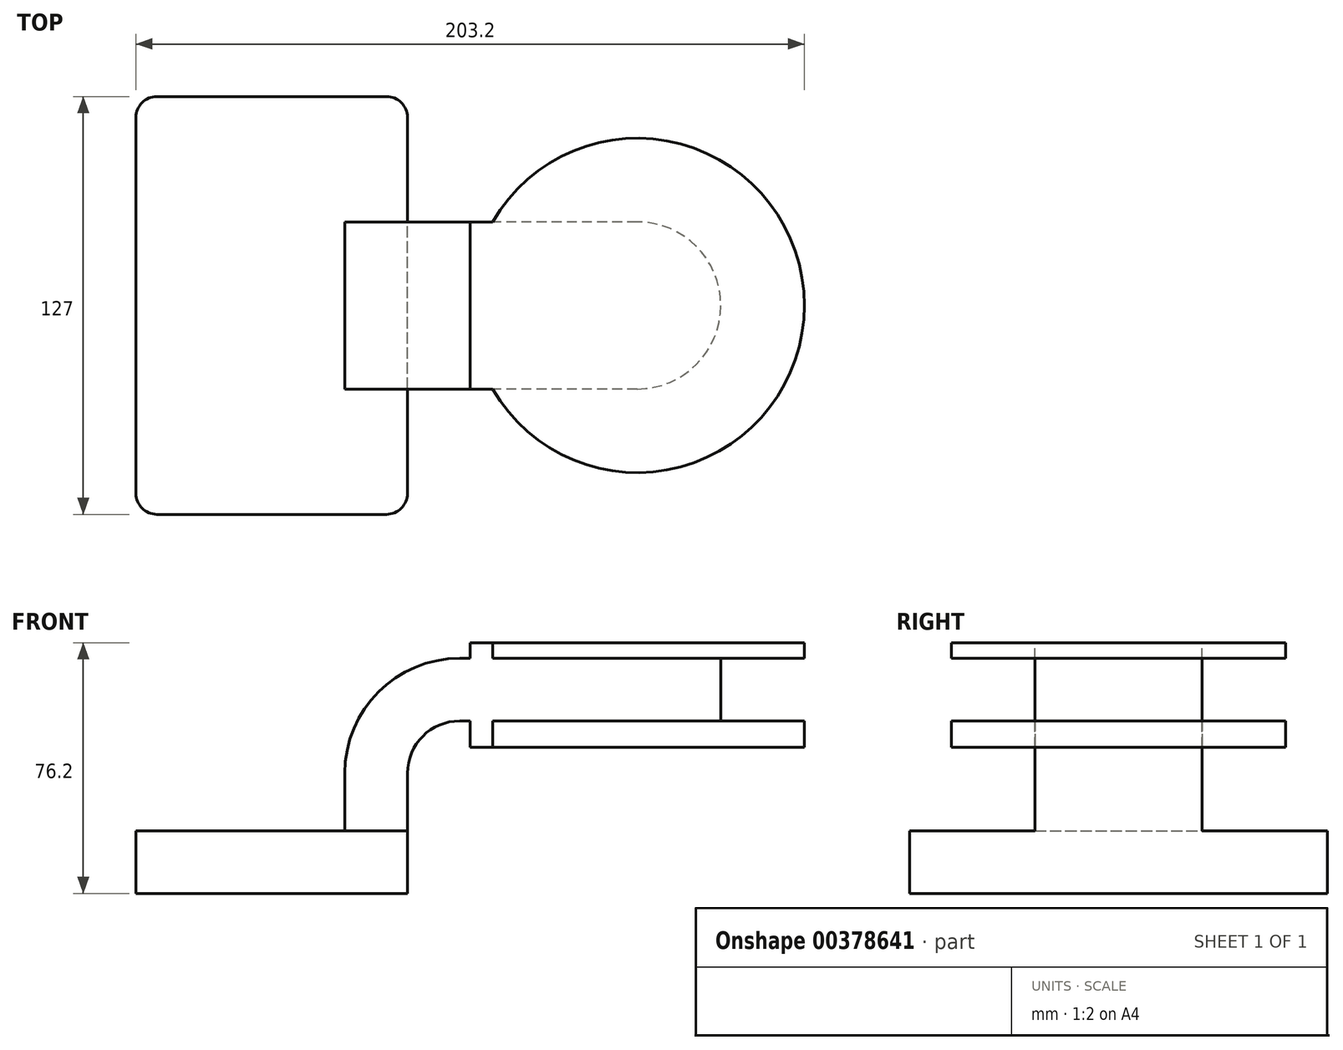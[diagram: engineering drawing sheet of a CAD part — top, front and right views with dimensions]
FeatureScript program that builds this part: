
annotation { "Feature Type Name" : "Feature", "Feature Type Description" : "" }
export const myFeature = defineFeature(function(context is Context, id is Id, definition is map)
    precondition{}
    {
        {
            var Q0;
            Q0=qCreatedBy(makeId("Front.planeOp"),FACE);
            var sketch = newSketch(context, id + "F0", { "sketchPlane" : qUnion([Q0])});
            skLineSegment(sketch, "E0.bottom", {"start": v(-41.27, -9.53) * mm, "end": v(41.28, -9.53) * mm});
            skLineSegment(sketch, "E0.top", {"start": v(-41.28, 9.53) * mm, "end": v(41.28, 9.53) * mm});
            skLineSegment(sketch, "E0.left", {"start": v(-41.28, -9.53) * mm, "end": v(-41.28, 9.53) * mm});
            skLineSegment(sketch, "E0.right", {"start": v(41.28, -9.53) * mm, "end": v(41.28, 9.53) * mm});
            skPoint(sketch, "E0.middle", {"position": v(0, 0) * mm});
            skLineSegment(sketch, "E1.bottom", {"start": v(111.13, 34.92) * mm, "end": v(60.33, 34.92) * mm});
            skLineSegment(sketch, "E1.top", {"start": v(111.13, 66.67) * mm, "end": v(60.33, 66.67) * mm});
            skLineSegment(sketch, "E1.left", {"start": v(111.13, 34.92) * mm, "end": v(111.13, 66.68) * mm});
            skLineSegment(sketch, "E1.right", {"start": v(60.33, 34.92) * mm, "end": v(60.33, 66.67) * mm});
            skPoint(sketch, "E1.middle", {"position": v(85.73, 50.8) * mm});
            skLineSegment(sketch, "E2", {"start": v(41.27, 9.52) * mm, "end": v(41.27, 27) * mm});
            skArc(sketch, "E3", {"start": v(41.27, 27) * mm, "mid": v(45.92, 38.23) * mm, "end": v(57.15, 42.88) * mm});
            skLineSegment(sketch, "E4", {"start": v(57.15, 42.88) * mm, "end": v(85.73, 42.88) * mm});
            skLineSegment(sketch, "E5.0", {"start": v(57.15, 61.93) * mm, "end": v(85.73, 61.93) * mm});
            skArc(sketch, "E5.1", {"start": v(22.22, 27) * mm, "mid": v(32.45, 51.7) * mm, "end": v(57.15, 61.93) * mm});
            skLineSegment(sketch, "E5.2", {"start": v(22.22, 9.52) * mm, "end": v(22.22, 27) * mm});
            skLineSegment(sketch, "E6", {"start": v(85.73, 42.88) * mm, "end": v(85.73, 61.93) * mm});
            skFitSpline(sketch, "E7", {"points": [v(-41.28, 9.53) * mm, v(57.15, 61.93) * mm], "startDerivative": vector(40.35, 93.42) * mm, "endDerivative": vector(155.44, -9.9) * mm});
            skSolve(sketch);
        }
        {
            var Q0;
            Q0=makeQuery(id+"F0.imprint","IMPRINT",FACE,{"disambiguationData":[TD([[makeQuery(id+"F0.imprint","IMPRINT",EDGE,{"derivedFrom":sQuery(id+"F0.wireOp",EDGE,"E0.bottom")}),1.0]])]});
            extrude(context, id + "F1", {"entities" : qUnion([Q0]), "endBound" : BoundingType.SYMMETRIC, "depth" : 127 * mm});
        }
        {
            var Q0;
            {var subQ1=sQuery(id+"F0.wireOp",EDGE,"E1.bottom");Q0=makeQuery(id+"F0.imprint","IMPRINT",FACE,{"disambiguationData":[TD([[makeQuery(id+"F0.imprint","IMPRINT",EDGE,{"derivedFrom":subQ1}),-1.0]])]});}
            var Q1;
            {var subQ0=sQuery(id+"F0.wireOp",EDGE,"E2");Q1=makeQuery(id+"F0.imprint","IMPRINT",FACE,{"disambiguationData":[TD([[makeQuery(id+"F0.imprint","IMPRINT",EDGE,{"derivedFrom":subQ0}),1.0]])]});}
            var Q2;
            {var subQ5=sQuery(id+"F0.wireOp",EDGE,"E6");Q2=makeQuery(id+"F0.imprint","IMPRINT",FACE,{"disambiguationData":[TD([[makeQuery(id+"F0.imprint","IMPRINT",EDGE,{"derivedFrom":subQ5}),1.0]])]});}
            extrude(context, id + "F2", {"entities" : qUnion([Q0, Q1, Q2]), "operationType" : NewBodyOperationType.ADD, "endBound" : BoundingType.SYMMETRIC, "depth" : 50.8 * mm});
        }
        {
            var Q0;
            Q0=makeQuery(id+"F0.imprint","IMPRINT",FACE,{"disambiguationData":[TD([[makeQuery(id+"F0.imprint","IMPRINT",EDGE,{"derivedFrom":sQuery(id+"F0.wireOp",EDGE,"E5.1")}),1.0]])]});
            extrude(context, id + "F3", {"entities" : qUnion([Q0]), "operationType" : NewBodyOperationType.ADD, "depth" : 15.88 * mm});
        }
        {
            var Q0;
            {var subQ1=sQuery(id+"F0.wireOp",EDGE,"E1.bottom");Q0=makeQuery(id+"F0.imprint","IMPRINT",FACE,{"disambiguationData":[TD([[makeQuery(id+"F0.imprint","IMPRINT",EDGE,{"derivedFrom":subQ1}),-1.0]])]});}
            var Q1;
            Q1=sQuery(id+"F0.wireOp",EDGE,"E1.left");
            revolve(context, id + "F4", {"operationType" : NewBodyOperationType.ADD, "entities" : qUnion([Q0]), "axis" : qUnion([Q1]), "revolveType" : RevolveType.FULL});
        }
        {
            var Q0;
            Q0=makeQuery(id+"F1.opExtrude","CAP_EDGE",EDGE,{"disambiguationData":[OSD([sQuery(id+"F0.wireOp",EDGE,"E0.left")])],"isStart":false});
            var Q1;
            Q1=makeQuery(id+"F1.opExtrude","CAP_EDGE",EDGE,{"disambiguationData":[OSD([sQuery(id+"F0.wireOp",EDGE,"E0.right")])],"isStart":false});
            var Q2;
            Q2=makeQuery(id+"F1.opExtrude","CAP_EDGE",EDGE,{"disambiguationData":[OSD([sQuery(id+"F0.wireOp",EDGE,"E0.right")])],"isStart":true});
            var Q3;
            Q3=makeQuery(id+"F1.opExtrude","CAP_EDGE",EDGE,{"disambiguationData":[OSD([sQuery(id+"F0.wireOp",EDGE,"E0.left")])],"isStart":true});
            fillet(context, id + "F5", {"entities" : qUnion([Q0, Q1, Q2, Q3]), "radius" : 6.35 * mm, "tangentPropagation" : true, "allowEdgeOverflow" : false});
        }
    });
